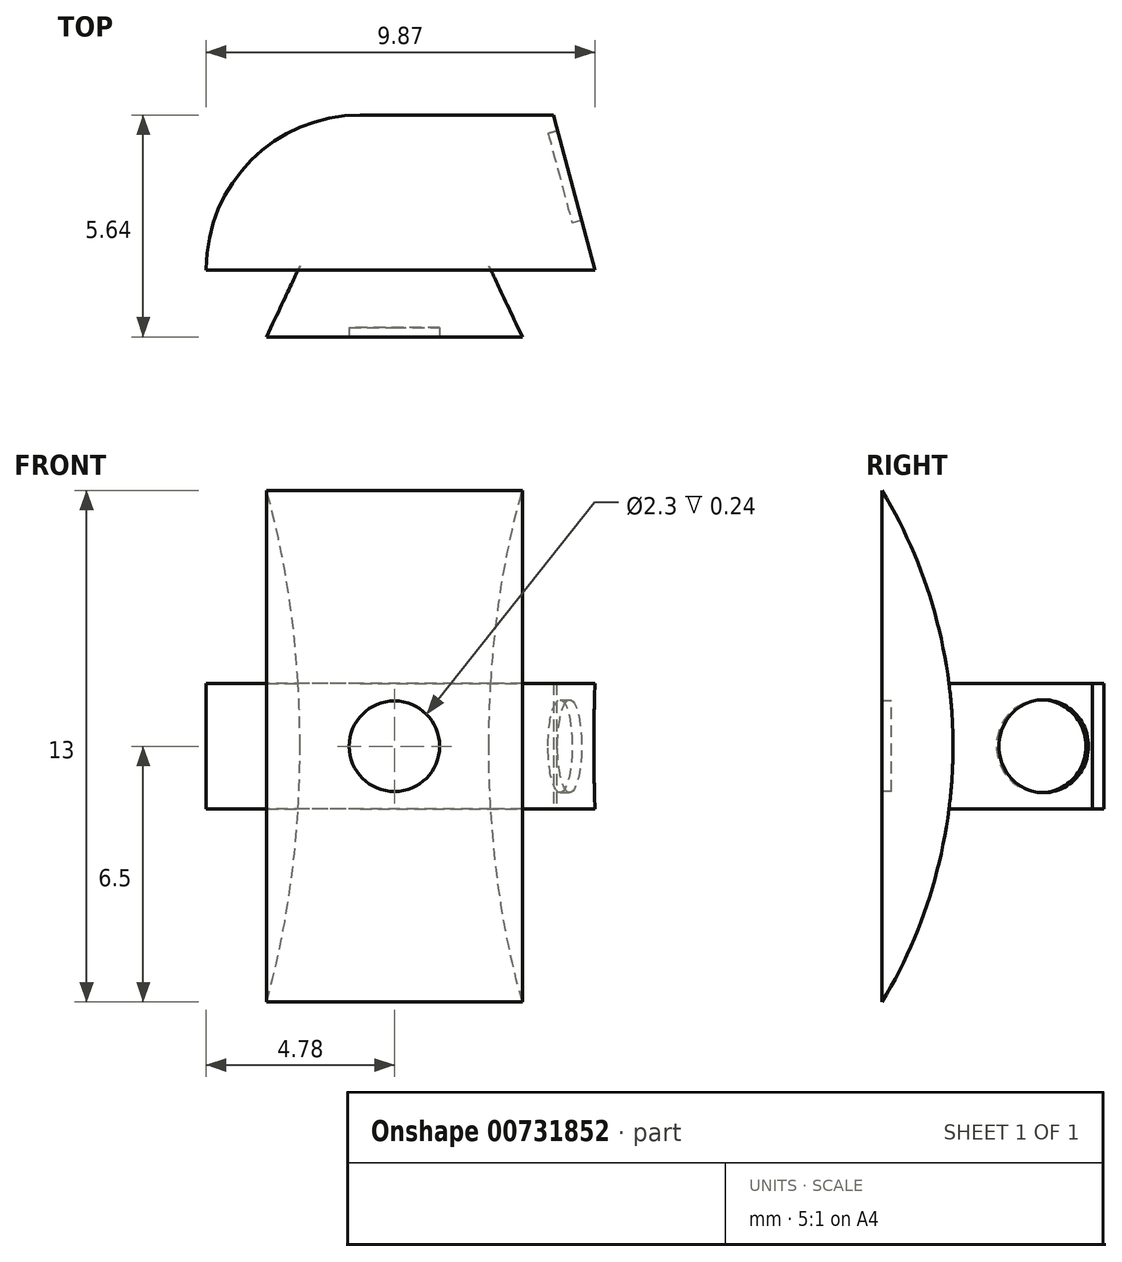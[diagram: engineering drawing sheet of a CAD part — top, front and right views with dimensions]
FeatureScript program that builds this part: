
annotation { "Feature Type Name" : "Feature", "Feature Type Description" : "" }
export const myFeature = defineFeature(function(context is Context, id is Id, definition is map)
    precondition{}
    {
        {
            var Q0;
            Q0=qCreatedBy(makeId("Top.planeOp"),FACE);
            var sketch = newSketch(context, id + "F0", { "sketchPlane" : qUnion([Q0])});
            skLineSegment(sketch, "E0", {"start": v(0, 0) * mm, "end": v(0, -1.8) * mm});
            skLineSegment(sketch, "E1", {"start": v(0, -1.8) * mm, "end": v(3.25, -1.8) * mm});
            skLineSegment(sketch, "E2", {"start": v(0, -1.8) * mm, "end": v(-3.25, -1.8) * mm});
            skLineSegment(sketch, "E3", {"start": v(0, 0) * mm, "end": v(-2.4, 0) * mm});
            skLineSegment(sketch, "E4", {"start": v(-2.4, 0) * mm, "end": v(0, 0) * mm});
            skLineSegment(sketch, "E5", {"start": v(0, 0) * mm, "end": v(2.4, 0) * mm});
            skLineSegment(sketch, "E6", {"start": v(2.4, 0) * mm, "end": v(3.25, -1.8) * mm});
            skLineSegment(sketch, "E7", {"start": v(-2.4, 0) * mm, "end": v(-3.25, -1.8) * mm});
            skSolve(sketch);
        }
        {
            var Q0;
            Q0=makeQuery(id+"F0.imprint","IMPRINT",FACE,{"disambiguationData":[TD([[makeQuery(id+"F0.imprint","IMPRINT",EDGE,{"derivedFrom":sQuery(id+"F0.wireOp",EDGE,"E0")}),1.0]])]});
            var Q1;
            Q1=makeQuery(id+"F0.imprint","IMPRINT",FACE,{"disambiguationData":[TD([[makeQuery(id+"F0.imprint","IMPRINT",EDGE,{"derivedFrom":sQuery(id+"F0.wireOp",EDGE,"E0")}),-1.0]])]});
            extrude(context, id + "F1", {"entities" : qUnion([Q0, Q1]), "depth" : 13 * mm, "offsetDistance" : 25 * mm});
        }
        {
            var Q0;
            Q0=makeQuery(id+"F1.opExtrude","CAP_EDGE",EDGE,{"disambiguationData":[OSD([sQuery(id+"F0.wireOp",EDGE,"E4"),sQuery(id+"F0.wireOp",EDGE,"E5")])],"isStart":true});
            var Q1;
            Q1=makeQuery(id+"F1.opExtrude","CAP_EDGE",EDGE,{"disambiguationData":[OSD([sQuery(id+"F0.wireOp",EDGE,"E4"),sQuery(id+"F0.wireOp",EDGE,"E5")])],"isStart":false});
            fillet(context, id + "F2", {"entities" : qUnion([Q0, Q1]), "radius" : 12.67 * mm, "tangentPropagation" : true, "allowEdgeOverflow" : false});
        }
        {
            var Q0;
            Q0=makeQuery(id+"F1.opExtrude","SWEPT_FACE",FACE,{"disambiguationData":[OSD([sQuery(id+"F0.wireOp",EDGE,"E1"),sQuery(id+"F0.wireOp",EDGE,"E2")])]});
            var sketch = newSketch(context, id + "F3", { "sketchPlane" : qUnion([Q0])});
            skLineSegment(sketch, "E8.bottom", {"start": v(3.25, 13) * mm, "end": v(-3.25, 13) * mm});
            skLineSegment(sketch, "E8.top", {"start": v(3.25, 0) * mm, "end": v(-3.25, 0) * mm});
            skLineSegment(sketch, "E8.left", {"start": v(3.25, 13) * mm, "end": v(3.25, 0) * mm});
            skLineSegment(sketch, "E8.right", {"start": v(-3.25, 13) * mm, "end": v(-3.25, 0) * mm});
            skPoint(sketch, "E8.middle", {"position": v(0, 6.5) * mm});
            skCircle(sketch, "E9", {"center": v(0, 6.5) * mm, "radius": 1.15 * mm});
            skSolve(sketch);
        }
        {
            var Q0;
            Q0=makeQuery(id+"F3.imprint","IMPRINT",FACE,{"disambiguationData":[TD([[makeQuery(id+"F3.imprint","IMPRINT",EDGE,{"derivedFrom":sQuery(id+"F3.wireOp",EDGE,"E9")}),1.0]])]});
            extrude(context, id + "F4", {"entities" : qUnion([Q0]), "operationType" : NewBodyOperationType.REMOVE, "oppositeDirection" : true, "depth" : 0.24 * mm, "offsetDistance" : 25 * mm});
        }
        {
            var Q0;
            Q0=qCreatedBy(makeId("Top.planeOp"),FACE);
            cPlane(context, id + "F5", {"entities" : qUnion([Q0]), "cplaneType" : CPlaneType.OFFSET, "offset" : 6.5 * mm, "width" : 150 * mm, "height" : 150 * mm});
        }
        {
            var Q0;
            Q0=qCreatedBy(id+"F5.planeOp",FACE);
            var sketch = newSketch(context, id + "F6", { "sketchPlane" : qUnion([Q0])});
            skLineSegment(sketch, "E10.bottom", {"start": v(-1.78, -1.06) * mm, "end": v(1.97, -1.06) * mm});
            skLineSegment(sketch, "E10.top", {"start": v(-1.78, 3.54) * mm, "end": v(1.97, 3.54) * mm});
            skLineSegment(sketch, "E10.left", {"start": v(-1.78, -1.06) * mm, "end": v(-1.78, 3.54) * mm});
            skLineSegment(sketch, "E10.right", {"start": v(1.97, -1.06) * mm, "end": v(1.97, 3.54) * mm});
            skSolve(sketch);
        }
        {
            var Q0;
            Q0=makeQuery(id+"F6.imprint","IMPRINT",FACE,{"disambiguationData":[TD([[makeQuery(id+"F6.imprint","IMPRINT",EDGE,{"derivedFrom":sQuery(id+"F6.wireOp",EDGE,"E10.bottom")}),1.0]])]});
            extrude(context, id + "F7", {"entities" : qUnion([Q0]), "operationType" : NewBodyOperationType.ADD, "endBound" : BoundingType.SYMMETRIC, "depth" : 3.2 * mm, "offsetDistance" : 25 * mm});
        }
        {
            var Q0;
            Q0=makeQuery(id+"F7.opExtrude","SWEPT_FACE",FACE,{"disambiguationData":[OSD([sQuery(id+"F6.wireOp",EDGE,"E10.right")])]});
            extrude(context, id + "F8", {"entities" : qUnion([Q0]), "operationType" : NewBodyOperationType.ADD, "depth" : 3.15 * mm, "offsetDistance" : 25 * mm});
        }
        {
            var Q0;
            Q0=makeQuery(id+"F8.opExtrude","CAP_EDGE",EDGE,{"disambiguationData":[OSD([sQuery(id+"F6.wireOp",EDGE,"E10.top"),sQuery(id+"F6.wireOp",EDGE,"E10.right")])],"isStart":false});
            chamfer(context, id + "F9", {"entities" : qUnion([Q0]), "chamferType" : ChamferType.OFFSET_ANGLE, "width" : 1 * mm, "oppositeDirection" : false, "angle" : 75 * degree, "tangentPropagation" : true});
        }
        {
            var Q0;
            Q0=makeQuery(id+"F9.opChamfer","BLEND_FACE",FACE,{"disambiguationData":[OSD([sQuery(id+"F6.wireOp",EDGE,"E10.top"),sQuery(id+"F6.wireOp",EDGE,"E10.right")])]});
            var sketch = newSketch(context, id + "F10", { "sketchPlane" : qUnion([Q0])});
            skLineSegment(sketch, "E11.bottom", {"start": v(2.35, 4.9) * mm, "end": v(-0.2, 4.9) * mm});
            skLineSegment(sketch, "E11.top", {"start": v(2.35, 8.1) * mm, "end": v(-0.2, 8.1) * mm});
            skLineSegment(sketch, "E11.left", {"start": v(2.35, 4.9) * mm, "end": v(2.35, 8.1) * mm});
            skLineSegment(sketch, "E11.right", {"start": v(-0.2, 4.9) * mm, "end": v(-0.2, 8.1) * mm});
            skPoint(sketch, "E11.middle", {"position": v(1.07, 6.5) * mm});
            skCircle(sketch, "E12", {"center": v(1.07, 6.5) * mm, "radius": 1.18 * mm});
            skSolve(sketch);
        }
        {
            var Q0;
            Q0=makeQuery(id+"F7.opExtrude","SWEPT_FACE",FACE,{"disambiguationData":[OSD([sQuery(id+"F6.wireOp",EDGE,"E10.left")])]});
            extrude(context, id + "F11", {"entities" : qUnion([Q0]), "operationType" : NewBodyOperationType.ADD, "depth" : 3 * mm, "offsetDistance" : 25 * mm});
        }
        {
            var Q0;
            Q0=makeQuery(id+"F10.imprint","IMPRINT",FACE,{"disambiguationData":[TD([[makeQuery(id+"F10.imprint","IMPRINT",EDGE,{"derivedFrom":sQuery(id+"F10.wireOp",EDGE,"E12")}),1.0]])]});
            extrude(context, id + "F12", {"entities" : qUnion([Q0]), "operationType" : NewBodyOperationType.REMOVE, "oppositeDirection" : true, "depth" : 0.25 * mm, "offsetDistance" : 25 * mm});
        }
        {
            var Q0;
            {var subQ0=sQuery(id+"F6.wireOp",EDGE,"E10.top");Q0=makeQuery(id+"F11.boolean.opBoolean","MERGE",FACE,{"derivedFrom":[makeQuery(id+"F8.boolean.opBoolean","MERGE",FACE,{"derivedFrom":[makeQuery(id+"F7.opExtrude","SWEPT_FACE",FACE,{"disambiguationData":[OSD([subQ0])]}),makeQuery(id+"F8.opExtrude","SWEPT_FACE",FACE,{"disambiguationData":[OSD([subQ0,sQuery(id+"F6.wireOp",EDGE,"E10.right")])]})]}),makeQuery(id+"F11.opExtrude","SWEPT_FACE",FACE,{"disambiguationData":[OSD([subQ0,sQuery(id+"F6.wireOp",EDGE,"E10.left")])]})]});}
            extrude(context, id + "F13", {"entities" : qUnion([Q0]), "operationType" : NewBodyOperationType.ADD, "depth" : 0.3 * mm, "offsetDistance" : 25 * mm});
        }
        {
            var Q0;
            Q0=makeQuery(id+"F13.opExtrude","CAP_EDGE",EDGE,{"disambiguationData":[OSD([sQuery(id+"F6.wireOp",EDGE,"E10.top"),sQuery(id+"F6.wireOp",EDGE,"E10.right")])],"isStart":false});
            chamfer(context, id + "F14", {"entities" : qUnion([Q0]), "chamferType" : ChamferType.OFFSET_ANGLE, "width" : 0.08 * mm, "oppositeDirection" : false, "angle" : 75 * degree, "tangentPropagation" : true});
        }
        {
            var Q0;
            Q0=makeQuery(id+"F13.opExtrude","CAP_EDGE",EDGE,{"disambiguationData":[OSD([sQuery(id+"F6.wireOp",EDGE,"E10.top"),sQuery(id+"F6.wireOp",EDGE,"E10.left")])],"isStart":false});
            fillet(context, id + "F15", {"entities" : qUnion([Q0]), "radius" : 3.91 * mm, "tangentPropagation" : true, "allowEdgeOverflow" : false});
        }
    });
